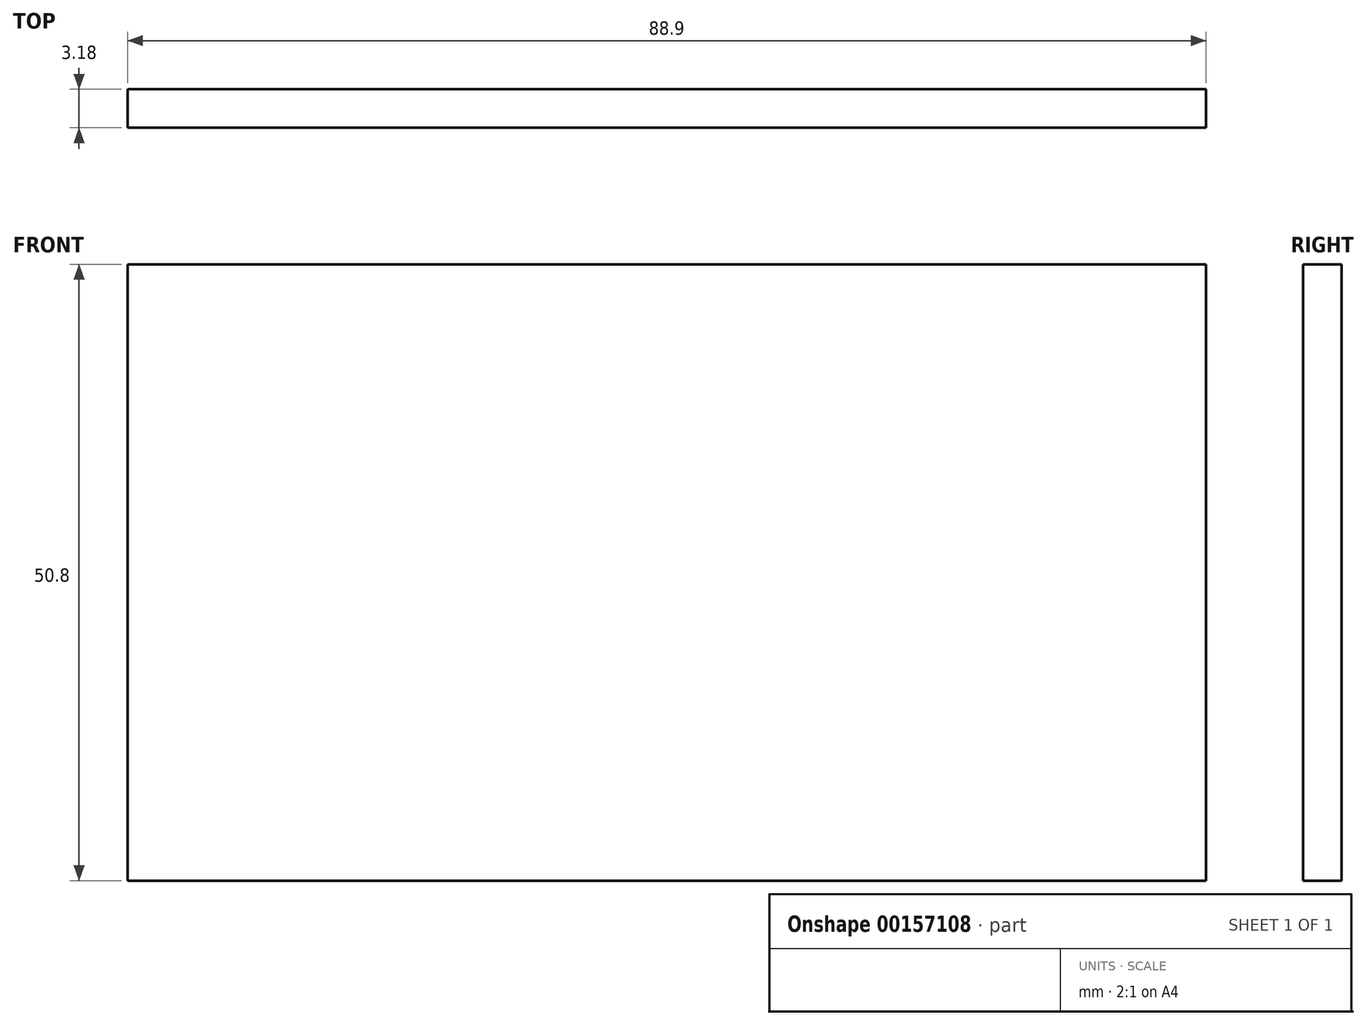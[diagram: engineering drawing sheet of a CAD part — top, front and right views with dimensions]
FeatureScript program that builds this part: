
annotation { "Feature Type Name" : "Feature", "Feature Type Description" : "" }
export const myFeature = defineFeature(function(context is Context, id is Id, definition is map)
    precondition{}
    {
        {
            var Q0;
            Q0=qCreatedBy(makeId("Front.planeOp"),FACE);
            var sketch = newSketch(context, id + "F0", { "sketchPlane" : qUnion([Q0])});
            skLineSegment(sketch, "E0", {"start": v(-43.8, -28.97) * mm, "end": v(45.1, -28.97) * mm});
            skLineSegment(sketch, "E1", {"start": v(-43.8, 21.83) * mm, "end": v(45.1, 21.83) * mm});
            skLineSegment(sketch, "E2", {"start": v(-43.8, 21.83) * mm, "end": v(-43.8, -28.97) * mm});
            skLineSegment(sketch, "E3", {"start": v(45.1, -28.97) * mm, "end": v(45.1, 21.83) * mm});
            skLineSegment(sketch, "E4", {"start": v(-43.8, 16.75) * mm, "end": v(45.1, 16.75) * mm});
            skLineSegment(sketch, "E5", {"start": v(-43.8, -23.9) * mm, "end": v(45.1, -23.9) * mm});
            skSolve(sketch);
        }
        {
            var Q0;
            Q0 = qSketchRegion(id + "F0", true);
            extrude(context, id + "F1", {"entities" : qUnion([Q0]), "endBound" : BoundingType.SYMMETRIC, "depth" : 3.17 * mm});
        }
    });
